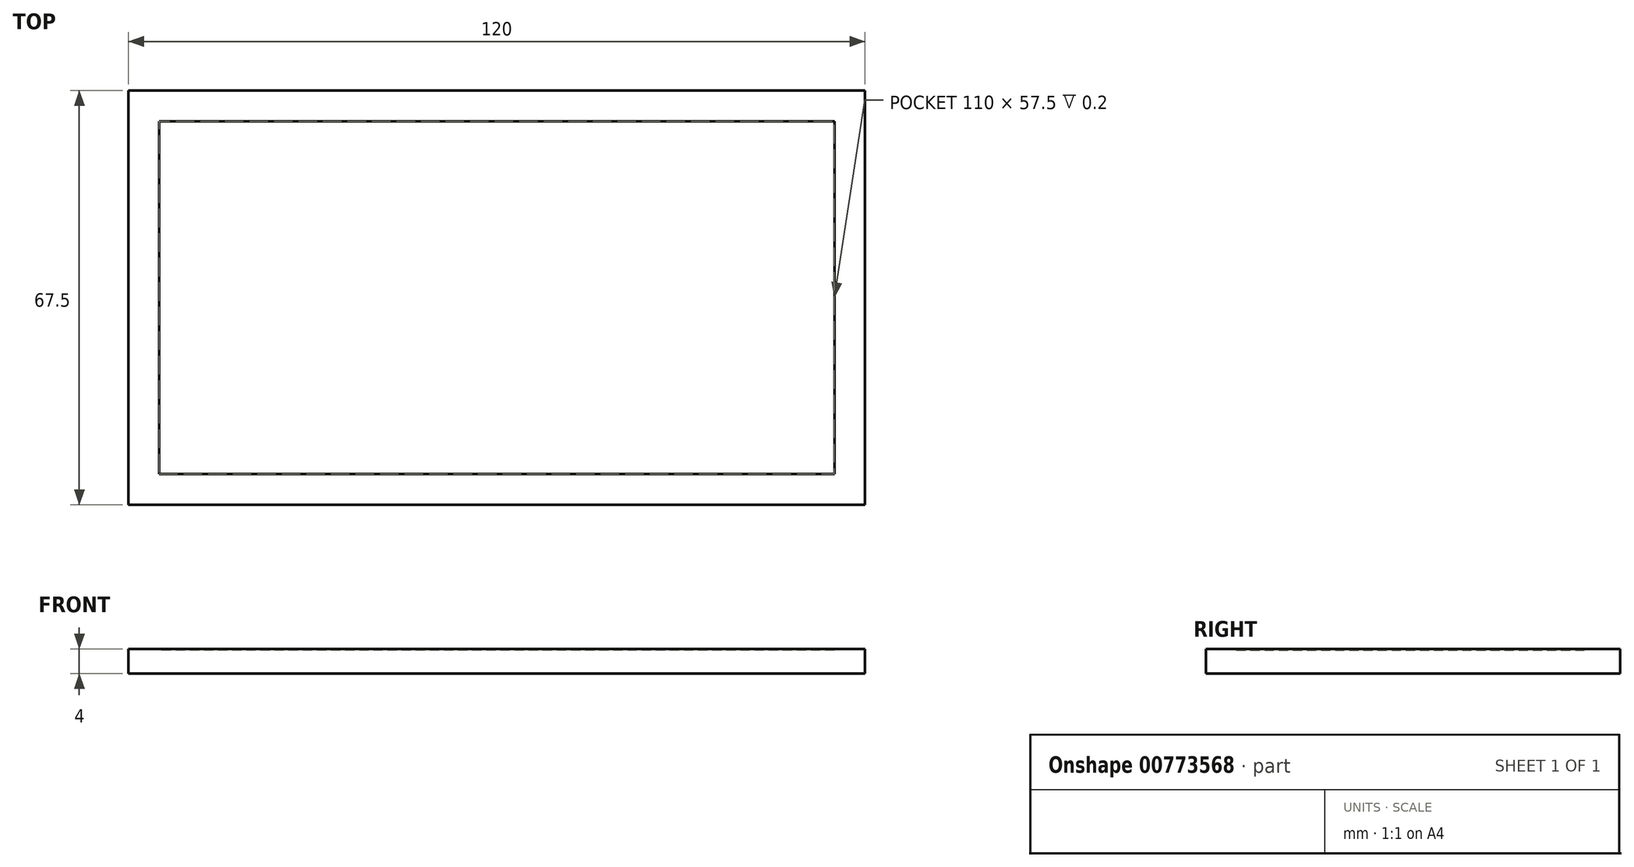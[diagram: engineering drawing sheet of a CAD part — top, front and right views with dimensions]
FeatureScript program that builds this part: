
annotation { "Feature Type Name" : "Feature", "Feature Type Description" : "" }
export const myFeature = defineFeature(function(context is Context, id is Id, definition is map)
    precondition{}
    {
        {
            var Q0;
            Q0=qCreatedBy(makeId("Top.planeOp"),FACE);
            var sketch = newSketch(context, id + "F0", { "sketchPlane" : qUnion([Q0])});
            skLineSegment(sketch, "E0.bottom", {"start": v(60, -33.75) * mm, "end": v(-60, -33.75) * mm});
            skLineSegment(sketch, "E0.top", {"start": v(60, 33.75) * mm, "end": v(-60, 33.75) * mm});
            skLineSegment(sketch, "E0.left", {"start": v(60, -33.75) * mm, "end": v(60, 33.75) * mm});
            skLineSegment(sketch, "E0.right", {"start": v(-60, -33.75) * mm, "end": v(-60, 33.75) * mm});
            skPoint(sketch, "E0.middle", {"position": v(0, 0) * mm});
            skLineSegment(sketch, "E1.0", {"start": v(55, 28.75) * mm, "end": v(-55, 28.75) * mm});
            skLineSegment(sketch, "E1.1", {"start": v(55, -28.75) * mm, "end": v(55, 28.75) * mm});
            skLineSegment(sketch, "E1.2", {"start": v(55, -28.75) * mm, "end": v(-55, -28.75) * mm});
            skLineSegment(sketch, "E1.3", {"start": v(-55, -28.75) * mm, "end": v(-55, 28.75) * mm});
            skSolve(sketch);
        }
        {
            var Q0;
            Q0=makeQuery(id+"F0.imprint","IMPRINT",FACE,{"disambiguationData":[TD([[makeQuery(id+"F0.imprint","IMPRINT",EDGE,{"derivedFrom":sQuery(id+"F0.wireOp",EDGE,"E0.bottom")}),-1.0]])]});
            var Q1;
            Q1=makeQuery(id+"F0.imprint","IMPRINT",FACE,{"disambiguationData":[TD([[makeQuery(id+"F0.imprint","IMPRINT",EDGE,{"derivedFrom":sQuery(id+"F0.wireOp",EDGE,"E1.0")}),1.0]])]});
            extrude(context, id + "F1", {"entities" : qUnion([Q0, Q1]), "depth" : 4 * mm, "offsetDistance" : 25 * mm});
        }
        {
            var Q0;
            Q0=makeQuery(id+"F1.opExtrude","CAP_FACE",FACE,{"disambiguationData":[OSD([sQuery(id+"F0.wireOp",EDGE,"E0.bottom"),sQuery(id+"F0.wireOp",EDGE,"E0.top"),sQuery(id+"F0.wireOp",EDGE,"E0.left"),sQuery(id+"F0.wireOp",EDGE,"E0.right")])],"isStart":false});
            var sketch = newSketch(context, id + "F2", { "sketchPlane" : qUnion([Q0])});
            skLineSegment(sketch, "E2.0", {"start": v(55, 28.75) * mm, "end": v(-55, 28.75) * mm});
            skLineSegment(sketch, "E2.1", {"start": v(-55, -28.75) * mm, "end": v(-55, 28.75) * mm});
            skLineSegment(sketch, "E2.2", {"start": v(55, -28.75) * mm, "end": v(-55, -28.75) * mm});
            skLineSegment(sketch, "E2.3", {"start": v(55, -28.75) * mm, "end": v(55, 28.75) * mm});
            skSolve(sketch);
        }
        {
            var Q0;
            Q0=makeQuery(id+"F2.imprint","IMPRINT",FACE,{"disambiguationData":[TD([[makeQuery(id+"F2.imprint","IMPRINT",EDGE,{"derivedFrom":sQuery(id+"F2.wireOp",EDGE,"E2.0")}),1.0]])]});
            extrude(context, id + "F3", {"entities" : qUnion([Q0]), "operationType" : NewBodyOperationType.REMOVE, "oppositeDirection" : true, "depth" : .2 * mm, "offsetDistance" : 25 * mm});
        }
    });
